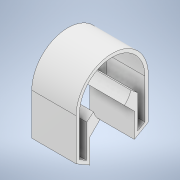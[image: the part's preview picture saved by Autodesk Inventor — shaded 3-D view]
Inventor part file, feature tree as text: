
AUTODESK INVENTOR PART (.ipt)
format: ipt  version: 2022.2 (Build 262287010, 287A)  size: 172,544 bytes
history: native  units: mm
features: extrude x2, sketch x1
ambient origin geometry x8: Origin, YZ Plane, XZ Plane, XY Plane, X Axis, Y Axis, Z Axis, Center Point
bodies: Body1 (feature_tree)
feature tree (3):
  sketch  "Sketch1"  dims[d0=130.0mm d2=75.0mm d3=120.0deg d4=35.0mm d9=30.0mm d10=50.0mm d11=45.0deg d12=60.0deg d13=40.0mm d14=3.682088mm d15=68.54732mm d16=70.044994mm d17=6.0mm d18=6.0mm d19=6.0mm d20=6.0mm d21=1.047198mm d22=15.809425mm d27=80.0mm d28=0.0mm d29=10.0mm d30=0.0mm d23=0.5mm d24=0.872665mm d25=0.5mm d26=0.872665mm]
  extrude  "Extrusion3"  Depth=10.0mm
  extrude  "Extrusion4"  TaperAngle=120.0deg  [1 undecoded]
note: 1 required parameter value undecoded (feature->parameter linkage not recoverable at this tier; creation-order binding heuristic only, values carry confidence <= 0.55)
